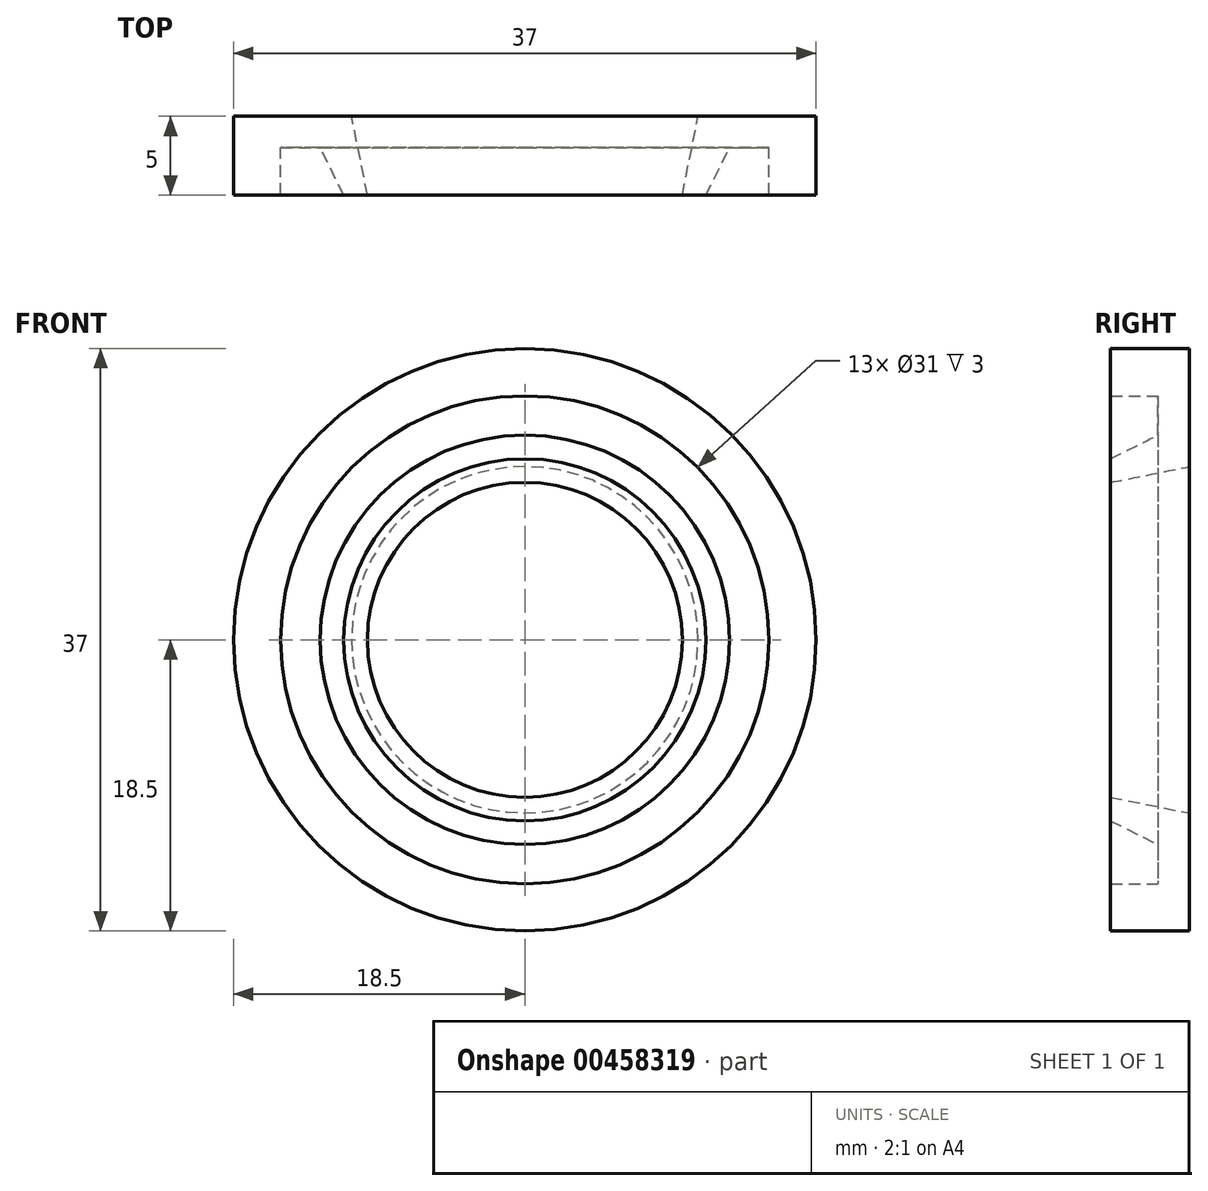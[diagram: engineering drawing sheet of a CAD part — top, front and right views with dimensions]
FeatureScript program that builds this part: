
annotation { "Feature Type Name" : "Feature", "Feature Type Description" : "" }
export const myFeature = defineFeature(function(context is Context, id is Id, definition is map)
    precondition{}
    {
        {
            var Q0;
            Q0=qCreatedBy(makeId("Right.planeOp"),FACE);
            var sketch = newSketch(context, id + "F0", { "sketchPlane" : qUnion([Q0])});
            skLineSegment(sketch, "E0", {"start": v(0, 0) * mm, "end": v(-14.73, 0) * mm, "construction": true});
            skLineSegment(sketch, "E1", {"start": v(0, 11) * mm, "end": v(0, 18.5) * mm});
            skLineSegment(sketch, "E2.MirrorCS", {"start": v(0, -11) * mm, "end": v(0, -18.5) * mm});
            skLineSegment(sketch, "E3", {"start": v(-5, 18.5) * mm, "end": v(-5, 15.5) * mm});
            skLineSegment(sketch, "E4.MirrorCS", {"start": v(-5, -18.5) * mm, "end": v(-5, -15.5) * mm});
            skLineSegment(sketch, "E5", {"start": v(0, 18.5) * mm, "end": v(-5, 18.5) * mm});
            skLineSegment(sketch, "E6", {"start": v(-5, 15.5) * mm, "end": v(-2, 15.5) * mm});
            skLineSegment(sketch, "E7.MirrorCS", {"start": v(-5, -15.5) * mm, "end": v(-2, -15.5) * mm});
            skLineSegment(sketch, "E8.MirrorCS", {"start": v(0, -18.5) * mm, "end": v(-5, -18.5) * mm});
            skLineSegment(sketch, "E9", {"start": v(-5, 11.5) * mm, "end": v(-5, 10) * mm});
            skLineSegment(sketch, "E10", {"start": v(-5, 11.5) * mm, "end": v(-2, 13) * mm});
            skLineSegment(sketch, "E11", {"start": v(-5, 10) * mm, "end": v(0, 11) * mm});
            skLineSegment(sketch, "E12.MirrorCS", {"start": v(-5, -10) * mm, "end": v(0, -11) * mm});
            skLineSegment(sketch, "E13.MirrorCS", {"start": v(-5, -11.5) * mm, "end": v(-5, -10) * mm});
            skLineSegment(sketch, "E14.MirrorCS", {"start": v(-5, -11.5) * mm, "end": v(-2, -13) * mm});
            skLineSegment(sketch, "E15", {"start": v(-2, -15.5) * mm, "end": v(-2, -13) * mm});
            skLineSegment(sketch, "E16.MirrorCS", {"start": v(-2, 15.5) * mm, "end": v(-2, 13) * mm});
            skSolve(sketch);
        }
        {
            var Q0;
            Q0=makeQuery(id+"F0.imprint","IMPRINT",FACE,{"disambiguationData":[TD([[makeQuery(id+"F0.imprint","IMPRINT",EDGE,{"derivedFrom":sQuery(id+"F0.wireOp",EDGE,"E1")}),1.0]])]});
            var Q1;
            Q1=sQuery(id+"F0.wireOp",EDGE,"E0");
            revolve(context, id + "F1", {"entities" : qUnion([Q0]), "axis" : qUnion([Q1]), "revolveType" : RevolveType.FULL});
        }
    });
